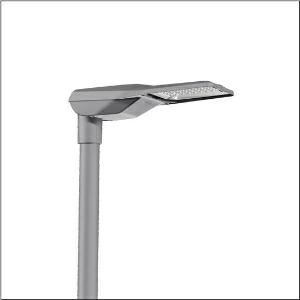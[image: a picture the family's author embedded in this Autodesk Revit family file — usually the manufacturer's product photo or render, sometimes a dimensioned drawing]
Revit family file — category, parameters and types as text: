
# Revit family: streetlight_sl_21_iq_mini___st0_5a_5xe2b31d08gb_9f53
name_source: partatom
category: Lighting Fixtures
units: mm (PartAtom-declared; Revit-internal decimal feet)

## family parameters
Cut with Voids When Loaded = No
Host = Face
Light Source = No
Part Type = Normal
Room Calculation Point = No
Round Connector Dimension = Use Diameter
Shared = No

## types (1)
- --- (1 x LED, 5680 lm, 37.1 W, 3000K)
    Apparent Load = 37 VA
    CIE Flux Codes = 41 75 97 100 100
    Color Rendering = 70
    Color Temperature = 3000K
    Default Elevation = 1800 mm
    Description = Streetlight SL 21 iQ mini, mast luminaire, primary light control with lens, of PMMA, primary optical cover: cover, of toughened safety glass, transparent, light distribution: ST0.5a, light emission: direct distribution, primary light characteristic: asymmetric, installation type: post-top, side-entry, LED, High Power LED, rated luminous flux: 5.680lm, luminous efficacy: 153lm/W, light colour: 730, colour temperature: 3000K, control gear: iQ-Comfort, control: Auto-Match, Temp-Guard, Lumen-Switch, Night-Set, Smart-Wire, Light-Fading, Desk-Remote (wireless, voltage-free reading and setting of iQ features in the workshop via application-optimized NFC function/RFID function), optimised constant luminous flux control (CLO 2.0), pre-setting: linear dimming characteristic, mains connection: 220..240V, AC, 50/60Hz, start of lifetime: 37W, end of service life: 39W, reduction: 18W, luminaire housing, of diecast aluminium, powder-coated, Siteco® metallic grey (DB 702S), corrosivity category C5 high according to DIN EN ISO 12944, please order mast flange separately, inclination adjustable: 0°, 5°, 10°, 15°, sealing non-destructively replaceable, multi-level sealing system, length: 628mm, width: 235mm, height: 110mm, mast flange for spigot size: 42mm (side-entry): 5XC10008XM4, 60/48mm (side-entry/post-top): 5XC10108XM2, 76/60mm (side-entry/post-top): 5XC10108XM1, mounting height: 4..8m, protection rating (complete): IP66, insulation class (complete): insulation class II (safety insulation), certification: CE, ENEC, ENEC+, VDE, impact resistance: IK10, permissible operating ambient temperature for outdoor applications: -40..+50°C, standard-compliant lighting for roads and squares, packaging unit: 1 piece

Light Distribution: ST0.5a
    Height = 110 mm
    Lamp = 1 x LED
    Lamp Light Flux = 5680 lm
    Lamp Power = 37.1 W
    Lamp count = 1
    Length = 625 mm
    Luminous efficacy = 153 lm/W
    Manufacturer = Siteco
    ModVariant = No
    Model = 5XE2B31D08GB
    Number of Poles = 1
    OnlyDefault = Yes
    Power Factor = 1
    Product Name = Streetlight SL 21 iQ mini | ST0.5a
    Product group = mast luminaire | pylon top
    ProductGroupID = 6100
    Protection Class = Protection class II
    Protection Degree = IP 66
    RLX_Detail_Level = 1
    RLX_Emergency_Light_Flux = 0 lm
    RLX_Emergency_Type = 0
    RLX_Emergency_Type_DB = No
    RlxData = <blob elided: 37337 chars, md5=2f00c67c>
    Socket = socket
    Standby Power = 0 W
    System Light Flux = 5680 lm
    System Power = 37 W
    Type Comments = factory setting: luminous flux: 100 % | dim-lin: 254 | 385 mA
    Type Image = l_1003519.jpg
    URL = http://relux.com
    VarID = @adj_192659
    Voltage = 0 V
    Weight = 0.00 kg
    Width = 234 mm

## geometry (parser evidence)
native form markers: Blend x4, Sweep x11
no freeform markers — native parametric forms only
